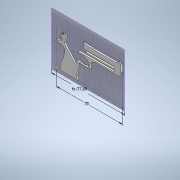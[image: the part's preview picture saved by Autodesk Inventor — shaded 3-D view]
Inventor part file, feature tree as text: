
AUTODESK INVENTOR PART (.ipt)
format: ipt  version: 2022 (Build 260153000, 153)  size: 3,211,264 bytes
history: native  units: in
note: dims shown in document units (in); Inventor stores cm internally (conversion verified against a paired STEP export)
features: other x9, sketch x7, reference x4, sheet_metal_op x3
ambient origin geometry x8: Origin, YZ Plane, XZ Plane, XY Plane, X Axis, Y Axis, Z Axis, Center Point
bodies: Body1 (feature_tree)
feature tree (23):
  sketch  "Sketch6"  dims[d94=3.0666in]
  sketch  "Sketch5"  dims[d93=0.2333in]
  sketch  "Sketch2"  dims[d25=2.7559in]
  sketch  "Sketch4"  dims[d87=0.2234in]
  sheet_metal_op  "Face4"
  sheet_metal_op  "Face5"
  other  "Image2"
  other  "Image4"
  other  "Image5"
  sketch  "Sketch7"  dims[d101=3.0666in]
  other  "Plate4"
  sketch  "Sketch8"  dims[d121=0.0591in]
  other  "Plate5"
  sheet_metal_op  "Bend1"
  sketch  "Sketch9"  dims[d125=0.0591in d126=0.0591in d127=0.0295in d128=0.1181in d129=0.0591in d130=0.0591in d131=0.0in]
  reference  "Reference1"
  reference  "Reference2"
  reference  "Reference3"
  reference  "Reference4"
  other  "Cut1"
  parser-record x1  (decoder bookkeeping rows leaked as tree rows — omitted from the tree; the rows remain in map.json)
  other  "Assembly1.iam"
  other  "sheetmettaal:2"
note: 1 file-system path scrubbed to <path> (originals preserved in map.json)
